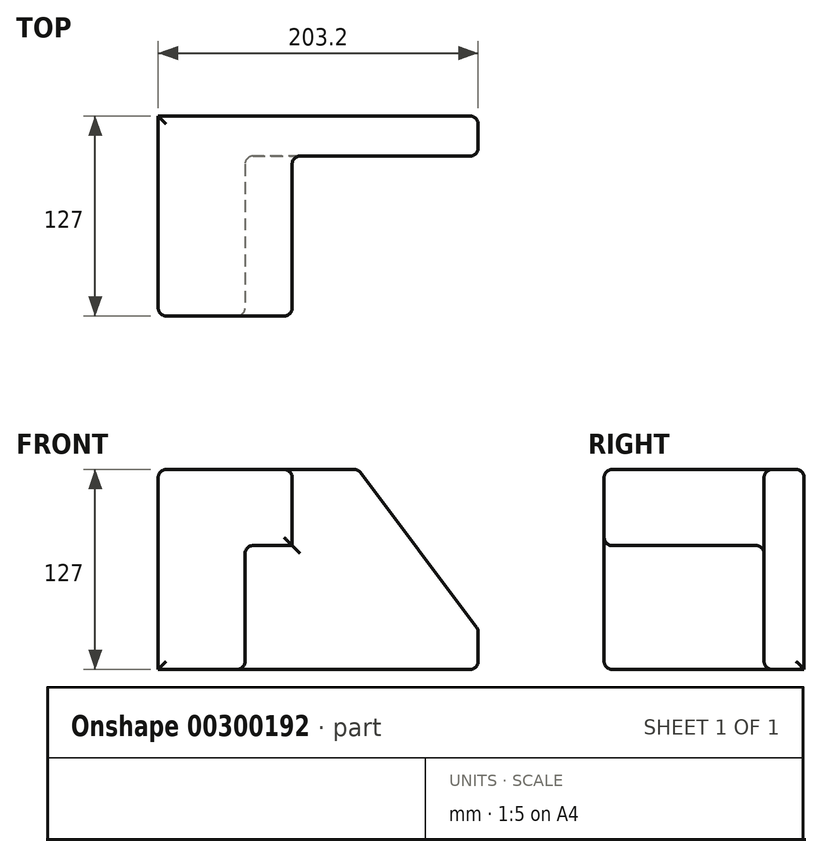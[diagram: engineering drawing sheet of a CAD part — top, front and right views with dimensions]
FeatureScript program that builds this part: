
annotation { "Feature Type Name" : "Feature", "Feature Type Description" : "" }
export const myFeature = defineFeature(function(context is Context, id is Id, definition is map)
    precondition{}
    {
        {
            var Q0;
            Q0=qCreatedBy(makeId("Front.planeOp"),FACE);
            var sketch = newSketch(context, id + "F0", { "sketchPlane" : qUnion([Q0])});
            skLineSegment(sketch, "E0.bottom", {"start": v(-140.5, -78.7) * mm, "end": v(62.7, -78.7) * mm});
            skLineSegment(sketch, "E0.top", {"start": v(-140.5, 48.3) * mm, "end": v(62.7, 48.3) * mm});
            skLineSegment(sketch, "E0.left", {"start": v(-140.5, -78.7) * mm, "end": v(-140.5, 48.3) * mm});
            skLineSegment(sketch, "E0.right", {"start": v(62.7, -78.7) * mm, "end": v(62.7, 48.3) * mm});
            skSolve(sketch);
        }
        {
            var Q0;
            Q0=makeQuery(id+"F0.imprint","IMPRINT",FACE,{"disambiguationData":[TD([[makeQuery(id+"F0.imprint","IMPRINT",EDGE,{"derivedFrom":sQuery(id+"F0.wireOp",EDGE,"E0.bottom")}),1.0]])]});
            extrude(context, id + "F1", {"entities" : qUnion([Q0]), "depth" : 127 * mm});
        }
        {
            var Q0;
            Q0=makeQuery(id+"F1.opExtrude","CAP_FACE",FACE,{"disambiguationData":[OSD([sQuery(id+"F0.wireOp",EDGE,"E0.bottom"),sQuery(id+"F0.wireOp",EDGE,"E0.top"),sQuery(id+"F0.wireOp",EDGE,"E0.left"),sQuery(id+"F0.wireOp",EDGE,"E0.right")])],"isStart":false});
            var sketch = newSketch(context, id + "F2", { "sketchPlane" : qUnion([Q0])});
            skLineSegment(sketch, "E1", {"start": v(-140.5, 48.3) * mm, "end": v(-55.46, 48.3) * mm});
            skLineSegment(sketch, "E2", {"start": v(-55.46, 48.3) * mm, "end": v(-55.46, 0) * mm});
            skLineSegment(sketch, "E3", {"start": v(-55.46, 0) * mm, "end": v(-85.36, 0) * mm});
            skLineSegment(sketch, "E4", {"start": v(-85.36, 0) * mm, "end": v(-85.36, -78.7) * mm});
            skLineSegment(sketch, "E5", {"start": v(-85.36, -78.7) * mm, "end": v(-140.5, -78.7) * mm});
            skLineSegment(sketch, "E6", {"start": v(-140.5, -78.7) * mm, "end": v(-140.5, 48.3) * mm});
            skSolve(sketch);
        }
        {
            var Q0;
            {var subQ3=sQuery(id+"F2.wireOp",EDGE,"E2");Q0=makeQuery(id+"F2.imprint","IMPRINT",FACE,{"disambiguationData":[TD([[makeQuery(id+"F2.imprint","IMPRINT",EDGE,{"derivedFrom":subQ3}),1.0]])]});}
            extrude(context, id + "F3", {"entities" : qUnion([Q0]), "operationType" : NewBodyOperationType.REMOVE, "oppositeDirection" : true, "depth" : 101.6 * mm});
        }
        {
            var Q0;
            Q0=makeQuery(id+"F1.opExtrude","SWEPT_EDGE",EDGE,{"disambiguationData":[OSD([sQuery(id+"F0.wireOp",EDGE,"E0.top"),sQuery(id+"F0.wireOp",EDGE,"E0.right")])]});
            chamfer(context, id + "F4", {"entities" : qUnion([Q0]), "chamferType" : ChamferType.TWO_OFFSETS, "width1" : 76.2 * mm, "oppositeDirection" : false, "width2" : 101.6 * mm, "tangentPropagation" : true});
        }
        {
            var Q0;
            Q0=makeQuery(id+"F3.boolean.opBoolean","COPY",EDGE,{"derivedFrom":makeQuery(id+"F3.opExtrude","SWEPT_EDGE",EDGE,{"disambiguationData":[OSD([sQuery(id+"F0.wireOp",EDGE,"E0.top"),sQuery(id+"F2.wireOp",EDGE,"E1"),sQuery(id+"F2.wireOp",EDGE,"E2")])]})});
            var Q1;
            Q1=makeQuery(id+"F3.boolean.opBoolean","COPY",EDGE,{"derivedFrom":makeQuery(id+"F3.opExtrude","CAP_EDGE",EDGE,{"disambiguationData":[OSD([sQuery(id+"F0.wireOp",EDGE,"E0.top")])],"isStart":false})});
            var Q2;
            {var subQ0=sQuery(id+"F0.wireOp",EDGE,"E0.top");Q2=makeQuery(id+"F4.opChamfer","BLEND_EDGE",EDGE,{"blendedFrom":[makeQuery(id+"F1.opExtrude","SWEPT_EDGE",EDGE,{"disambiguationData":[OSD([subQ0,sQuery(id+"F0.wireOp",EDGE,"E0.right")])]}),makeQuery(id+"F1.opExtrude","SWEPT_FACE",FACE,{"disambiguationData":[OSD([subQ0])]})],"blendedInto":[makeQuery(id+"F1.opExtrude","SWEPT_FACE",FACE,{"disambiguationData":[OSD([subQ0])]})]});}
            var Q3;
            {var subQ0=sQuery(id+"F0.wireOp",EDGE,"E0.right");Q3=makeQuery(id+"F4.opChamfer","BLEND_EDGE",EDGE,{"blendedFrom":[makeQuery(id+"F1.opExtrude","SWEPT_EDGE",EDGE,{"disambiguationData":[OSD([sQuery(id+"F0.wireOp",EDGE,"E0.top"),subQ0])]}),makeQuery(id+"F1.opExtrude","SWEPT_FACE",FACE,{"disambiguationData":[OSD([subQ0])]})],"blendedInto":[makeQuery(id+"F1.opExtrude","SWEPT_FACE",FACE,{"disambiguationData":[OSD([subQ0])]})]});}
            var Q4;
            {var subQ0=sQuery(id+"F0.wireOp",EDGE,"E0.right");var subQ1=sQuery(id+"F0.wireOp",EDGE,"E0.top");Q4=makeQuery(id+"F4.opChamfer","BLEND_EDGE",EDGE,{"blendedFrom":[makeQuery(id+"F1.opExtrude","SWEPT_EDGE",EDGE,{"disambiguationData":[OSD([subQ1,subQ0])]}),makeQuery(id+"F3.boolean.opBoolean","COPY",FACE,{"derivedFrom":makeQuery(id+"F3.opExtrude","CAP_FACE",FACE,{"disambiguationData":[OSD([sQuery(id+"F0.wireOp",EDGE,"E0.bottom"),subQ1,subQ0,sQuery(id+"F2.wireOp",EDGE,"E2"),sQuery(id+"F2.wireOp",EDGE,"E3"),sQuery(id+"F2.wireOp",EDGE,"E4")])],"isStart":false})})],"blendedInto":[makeQuery(id+"F3.boolean.opBoolean","COPY",FACE,{"derivedFrom":makeQuery(id+"F3.opExtrude","CAP_FACE",FACE,{"disambiguationData":[OSD([sQuery(id+"F0.wireOp",EDGE,"E0.bottom"),subQ1,subQ0,sQuery(id+"F2.wireOp",EDGE,"E2"),sQuery(id+"F2.wireOp",EDGE,"E3"),sQuery(id+"F2.wireOp",EDGE,"E4")])],"isStart":false})})]});}
            var Q5;
            {var subQ0=sQuery(id+"F0.wireOp",EDGE,"E0.right");var subQ1=sQuery(id+"F0.wireOp",EDGE,"E0.top");Q5=makeQuery(id+"F4.opChamfer","BLEND_EDGE",EDGE,{"blendedFrom":[makeQuery(id+"F1.opExtrude","SWEPT_EDGE",EDGE,{"disambiguationData":[OSD([subQ1,subQ0])]}),makeQuery(id+"F1.opExtrude","CAP_FACE",FACE,{"disambiguationData":[OSD([sQuery(id+"F0.wireOp",EDGE,"E0.bottom"),subQ1,sQuery(id+"F0.wireOp",EDGE,"E0.left"),subQ0])],"isStart":true})],"blendedInto":[makeQuery(id+"F1.opExtrude","CAP_FACE",FACE,{"disambiguationData":[OSD([sQuery(id+"F0.wireOp",EDGE,"E0.bottom"),subQ1,sQuery(id+"F0.wireOp",EDGE,"E0.left"),subQ0])],"isStart":true})]});}
            var Q6;
            Q6=makeQuery(id+"F3.boolean.opBoolean","COPY",EDGE,{"derivedFrom":makeQuery(id+"F3.opExtrude","CAP_EDGE",EDGE,{"disambiguationData":[OSD([sQuery(id+"F0.wireOp",EDGE,"E0.right")])],"isStart":false})});
            var Q7;
            Q7=makeQuery(id+"F1.opExtrude","SWEPT_EDGE",EDGE,{"disambiguationData":[OSD([sQuery(id+"F0.wireOp",EDGE,"E0.bottom"),sQuery(id+"F0.wireOp",EDGE,"E0.right")])]});
            var Q8;
            Q8=makeQuery(id+"F1.opExtrude","CAP_EDGE",EDGE,{"disambiguationData":[OSD([sQuery(id+"F0.wireOp",EDGE,"E0.right")])],"isStart":true});
            var Q9;
            Q9=makeQuery(id+"F3.boolean.opBoolean","COPY",FACE,{"derivedFrom":makeQuery(id+"F3.opExtrude","CAP_FACE",FACE,{"disambiguationData":[OSD([sQuery(id+"F0.wireOp",EDGE,"E0.bottom"),sQuery(id+"F0.wireOp",EDGE,"E0.top"),sQuery(id+"F0.wireOp",EDGE,"E0.right"),sQuery(id+"F2.wireOp",EDGE,"E2"),sQuery(id+"F2.wireOp",EDGE,"E3"),sQuery(id+"F2.wireOp",EDGE,"E4")])],"isStart":false})});
            var Q10;
            Q10=makeQuery(id+"F3.boolean.opBoolean","COPY",FACE,{"derivedFrom":makeQuery(id+"F3.opExtrude","SWEPT_FACE",FACE,{"disambiguationData":[OSD([sQuery(id+"F2.wireOp",EDGE,"E4")])]})});
            var Q11;
            Q11=makeQuery(id+"F1.opExtrude","CAP_FACE",FACE,{"disambiguationData":[OSD([sQuery(id+"F0.wireOp",EDGE,"E0.bottom"),sQuery(id+"F0.wireOp",EDGE,"E0.top"),sQuery(id+"F0.wireOp",EDGE,"E0.left"),sQuery(id+"F0.wireOp",EDGE,"E0.right")])],"isStart":false});
            var Q12;
            Q12=makeQuery(id+"F1.opExtrude","SWEPT_FACE",FACE,{"disambiguationData":[OSD([sQuery(id+"F0.wireOp",EDGE,"E0.top")])]});
            fillet(context, id + "F5", {"entities" : qUnion([Q0, Q1, Q2, Q3, Q4, Q5, Q6, Q7, Q8, Q9, Q10, Q11, Q12]), "radius" : 5.08 * mm, "tangentPropagation" : true, "allowEdgeOverflow" : false});
        }
    });
